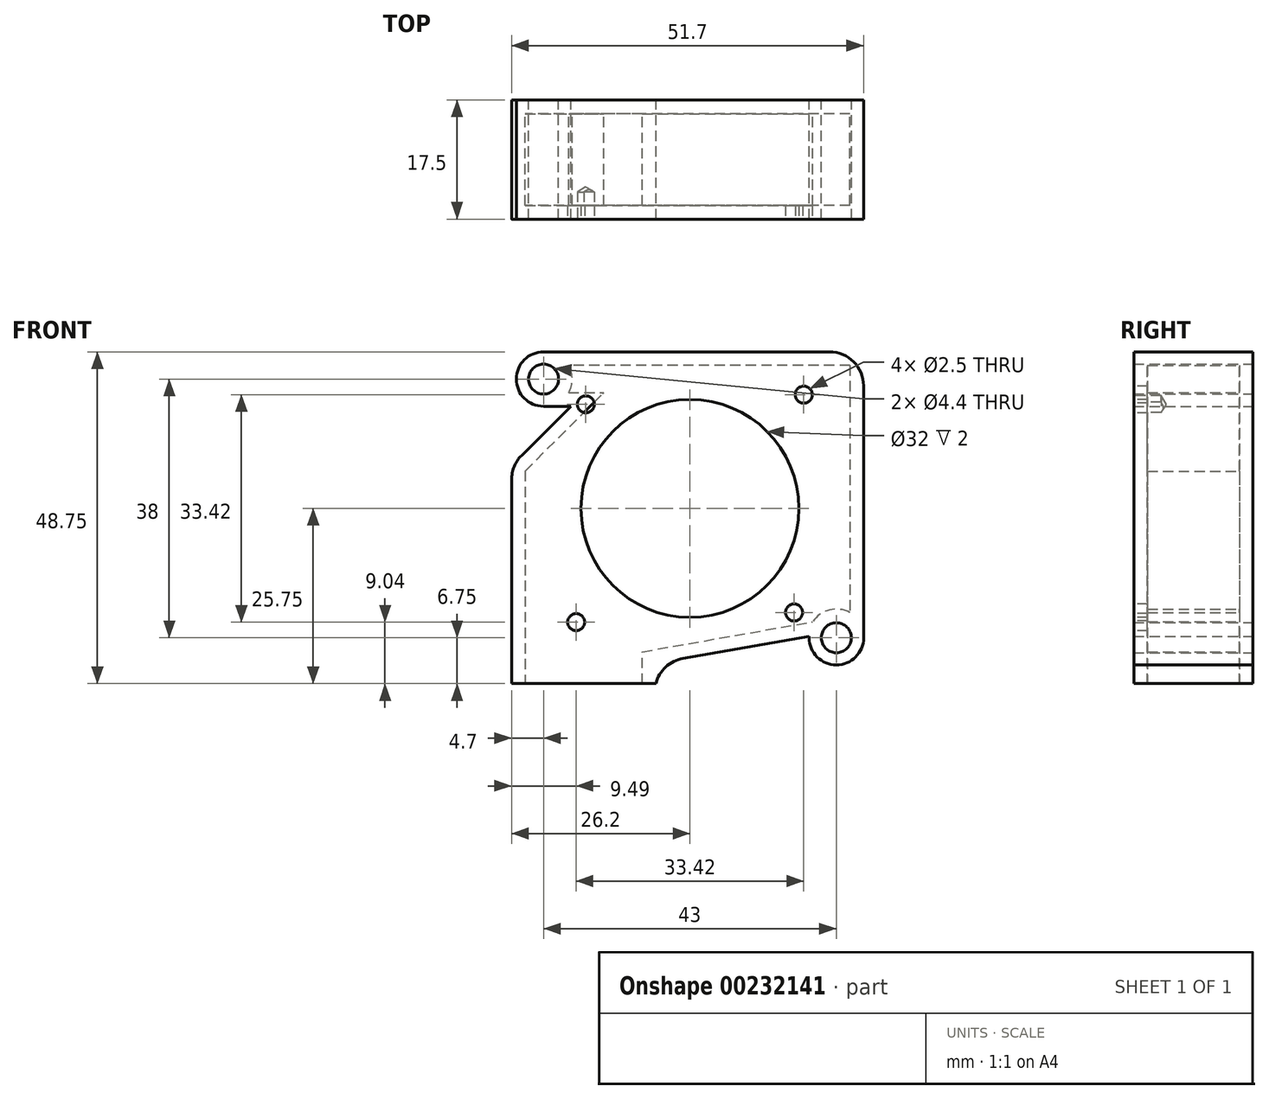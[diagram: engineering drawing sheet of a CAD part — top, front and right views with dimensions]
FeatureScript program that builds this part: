
annotation { "Feature Type Name" : "Feature", "Feature Type Description" : "" }
export const myFeature = defineFeature(function(context is Context, id is Id, definition is map)
    precondition{}
    {
        {
            var Q0;
            Q0=qCreatedBy(makeId("Front.planeOp"),FACE);
            var sketch = newSketch(context, id + "F0", { "sketchPlane" : qUnion([Q0])});
            skLineSegment(sketch, "E0.bottom", {"start": v(25.5, 23) * mm, "end": v(-21.5, 23) * mm});
            skLineSegment(sketch, "E0.left", {"start": v(25.5, 23) * mm, "end": v(25.5, -19) * mm});
            skPoint(sketch, "E0.middle", {"position": v(0, 0) * mm});
            skLineSegment(sketch, "E1.top", {"start": v(-21.5, 15) * mm, "end": v(17.5, 15) * mm});
            skLineSegment(sketch, "E1.right", {"start": v(17.5, -19) * mm, "end": v(17.5, 15) * mm});
            skCircle(sketch, "E2", {"center": v(-21.5, 19) * mm, "radius": 2.2 * mm});
            skCircle(sketch, "E3.MirrorC", {"center": v(21.5, -19) * mm, "radius": 2.2 * mm});
            skArc(sketch, "E4", {"start": v(-21.5, 23) * mm, "mid": v(-25.5, 19) * mm, "end": v(-21.5, 15) * mm});
            skPoint(sketch, "E5.orphan", {"position": v(-25.5, 23) * mm});
            skArc(sketch, "E6", {"start": v(17.5, -19) * mm, "mid": v(21.5, -23) * mm, "end": v(25.5, -19) * mm});
            skPoint(sketch, "E7.orphan", {"position": v(25.5, -23) * mm});
            skSolve(sketch);
        }
        {
            var Q0;
            Q0=makeQuery(id+"F0.imprint","IMPRINT",FACE,{"disambiguationData":[TD([[makeQuery(id+"F0.imprint","IMPRINT",EDGE,{"derivedFrom":sQuery(id+"F0.wireOp",EDGE,"E0.bottom")}),1.0]])]});
            extrude(context, id + "F1", {"entities" : qUnion([Q0]), "depth" : 17.5 * mm});
        }
        {
            var Q0;
            Q0=qCreatedBy(makeId("Front.planeOp"),FACE);
            var sketch = newSketch(context, id + "F2", { "sketchPlane" : qUnion([Q0])});
            skPoint(sketch, "E8.0", {"position": v(17.5, 15) * mm});
            skLineSegment(sketch, "E9.bottom", {"start": v(17.5, 15) * mm, "end": v(-17.5, 15) * mm});
            skLineSegment(sketch, "E9.top", {"start": v(-5, -25.75) * mm, "end": v(-26.2, -25.75) * mm});
            skLineSegment(sketch, "E9.left", {"start": v(17.5, 15) * mm, "end": v(17.5, -18.78) * mm});
            skLineSegment(sketch, "E9.right", {"start": v(-26.2, 6.3) * mm, "end": v(-26.2, -25.75) * mm});
            skLineSegment(sketch, "E10", {"start": v(-5, -25.75) * mm, "end": v(-5, -22.75) * mm});
            skLineSegment(sketch, "E11", {"start": v(-5, -22.75) * mm, "end": v(17.5, -18.78) * mm});
            skLineSegment(sketch, "E12", {"start": v(-26.2, 6.3) * mm, "end": v(-17.5, 15) * mm});
            skSolve(sketch);
        }
        {
            var Q0;
            Q0=makeQuery(id+"F2.imprint","IMPRINT",FACE,{"disambiguationData":[TD([[makeQuery(id+"F2.imprint","IMPRINT",EDGE,{"derivedFrom":sQuery(id+"F2.wireOp",EDGE,"E9.bottom")}),1.0]])]});
            var Q1;
            Q1=makeQuery(id+"F1.opExtrude","CAP_FACE",FACE,{"disambiguationData":[OSD([sQuery(id+"F0.wireOp",EDGE,"E0.bottom"),sQuery(id+"F0.wireOp",EDGE,"E0.left"),sQuery(id+"F0.wireOp",EDGE,"E1.top"),sQuery(id+"F0.wireOp",EDGE,"E1.right"),sQuery(id+"F0.wireOp",EDGE,"E2"),sQuery(id+"F0.wireOp",EDGE,"E3.MirrorC"),sQuery(id+"F0.wireOp",EDGE,"E4"),sQuery(id+"F0.wireOp",EDGE,"E6")])],"isStart":false});
            extrude(context, id + "F3", {"entities" : qUnion([Q0]), "operationType" : NewBodyOperationType.ADD, "endBound" : BoundingType.UP_TO_SURFACE, "endBoundEntityFace" : qUnion([Q1]), "depth" : 25 * mm});
        }
        {
            var Q0;
            Q0=makeQuery(id+"F3.opExtrude","SWEPT_FACE",FACE,{"disambiguationData":[OSD([sQuery(id+"F2.wireOp",EDGE,"E9.top")])]});
            shell(context, id + "F4", {"entities" : qUnion([Q0]), "thickness" : 2 * mm});
        }
        {
            var Q0;
            Q0=makeQuery(id+"F3.opExtrude","SWEPT_EDGE",EDGE,{"disambiguationData":[OSD([sQuery(id+"F2.wireOp",EDGE,"E9.right"),sQuery(id+"F2.wireOp",EDGE,"E12")])]});
            var Q1;
            Q1=makeQuery(id+"F3.opExtrude","SWEPT_EDGE",EDGE,{"disambiguationData":[OSD([sQuery(id+"F2.wireOp",EDGE,"E9.bottom"),sQuery(id+"F2.wireOp",EDGE,"E12")])]});
            var Q2;
            Q2=makeQuery(id+"F3.opExtrude","SWEPT_EDGE",EDGE,{"disambiguationData":[OSD([sQuery(id+"F2.wireOp",EDGE,"E9.left"),sQuery(id+"F2.wireOp",EDGE,"E11")])]});
            var Q3;
            Q3=makeQuery(id+"F1.opExtrude","SWEPT_EDGE",EDGE,{"disambiguationData":[OSD([sQuery(id+"F0.wireOp",EDGE,"E0.bottom"),sQuery(id+"F0.wireOp",EDGE,"E0.left")])]});
            var Q4;
            Q4=makeQuery(id+"F3.opExtrude","SWEPT_EDGE",EDGE,{"disambiguationData":[OSD([sQuery(id+"F2.wireOp",EDGE,"E10"),sQuery(id+"F2.wireOp",EDGE,"E11")])]});
            fillet(context, id + "F5", {"entities" : qUnion([Q0, Q1, Q2, Q3, Q4]), "radius" : 5 * mm, "tangentPropagation" : true, "allowEdgeOverflow" : false});
        }
        {
            var Q0;
            {var subQ0=sQuery(id+"F0.wireOp",EDGE,"E6");var subQ1=sQuery(id+"F0.wireOp",EDGE,"E4");var subQ2=sQuery(id+"F0.wireOp",EDGE,"E3.MirrorC");var subQ3=sQuery(id+"F0.wireOp",EDGE,"E2");var subQ4=sQuery(id+"F0.wireOp",EDGE,"E1.right");var subQ5=sQuery(id+"F0.wireOp",EDGE,"E1.top");var subQ6=sQuery(id+"F0.wireOp",EDGE,"E0.left");var subQ7=sQuery(id+"F0.wireOp",EDGE,"E0.bottom");Q0=makeQuery(id+"F3.boolean.opBoolean","MERGE",FACE,{"derivedFrom":[makeQuery(id+"F1.opExtrude","CAP_FACE",FACE,{"disambiguationData":[OSD([subQ7,subQ6,subQ5,subQ4,subQ3,subQ2,subQ1,subQ0])],"isStart":false}),makeQuery(id+"F3.opExtrude","CAP_FACE",FACE,{"disambiguationData":[OSD([subQ7,subQ6,subQ5,subQ4,subQ3,subQ2,subQ1,subQ0])],"isStart":false})]});}
            var sketch = newSketch(context, id + "F6", { "sketchPlane" : qUnion([Q0])});
            skPoint(sketch, "E13", {"position": v(0, 0) * mm});
            skLineSegment(sketch, "E14", {"start": v(0, 0) * mm, "end": v(-21.63, -21.63) * mm, "construction": true});
            skLineSegment(sketch, "E15", {"start": v(0, 0) * mm, "end": v(24.58, -24.58) * mm, "construction": true});
            skLineSegment(sketch, "E16", {"start": v(0, 0) * mm, "end": v(-20.98, 20.98) * mm, "construction": true});
            skLineSegment(sketch, "E17", {"start": v(0, 0) * mm, "end": v(27.65, 27.65) * mm, "construction": true});
            skPoint(sketch, "E18", {"position": v(-15.3, 15.3) * mm});
            skPoint(sketch, "E19", {"position": v(16.7, 16.7) * mm});
            skPoint(sketch, "E20", {"position": v(15.3, -15.3) * mm});
            skPoint(sketch, "E21", {"position": v(-16.7, -16.7) * mm});
            skSolve(sketch);
        }
        {
            var Q0;
            Q0=sQuery(id+"F6.wireOp",VERTEX,"E13");
            var Q1;
            Q1=makeQuery(id+"F1.opExtrude","SWEPT_BODY",BODY,{"disambiguationData":[OSD([sQuery(id+"F0.wireOp",EDGE,"E0.bottom"),sQuery(id+"F0.wireOp",EDGE,"E0.left"),sQuery(id+"F0.wireOp",EDGE,"E1.top"),sQuery(id+"F0.wireOp",EDGE,"E1.right"),sQuery(id+"F0.wireOp",EDGE,"E2"),sQuery(id+"F0.wireOp",EDGE,"E3.MirrorC"),sQuery(id+"F0.wireOp",EDGE,"E4"),sQuery(id+"F0.wireOp",EDGE,"E6")])]});
            hole(context, id + "F7", {"style" : HoleStyle.SIMPLE, "endStyle" : HoleEndStyle.BLIND, "holeDiameter" : 32 * mm, "holeDepth" : 4 * mm, "startFromSketch" : true, "locations" : qUnion([Q0]), "scope" : qUnion([Q1])});
        }
        {
            var Q0;
            Q0=sQuery(id+"F6.wireOp",VERTEX,"E18");
            var Q1;
            Q1=sQuery(id+"F6.wireOp",VERTEX,"E21");
            var Q2;
            Q2=sQuery(id+"F6.wireOp",VERTEX,"E20");
            var Q3;
            Q3=sQuery(id+"F6.wireOp",VERTEX,"E19");
            var Q4;
            Q4=makeQuery(id+"F1.opExtrude","SWEPT_BODY",BODY,{"disambiguationData":[OSD([sQuery(id+"F0.wireOp",EDGE,"E0.bottom"),sQuery(id+"F0.wireOp",EDGE,"E0.left"),sQuery(id+"F0.wireOp",EDGE,"E1.top"),sQuery(id+"F0.wireOp",EDGE,"E1.right"),sQuery(id+"F0.wireOp",EDGE,"E2"),sQuery(id+"F0.wireOp",EDGE,"E3.MirrorC"),sQuery(id+"F0.wireOp",EDGE,"E4"),sQuery(id+"F0.wireOp",EDGE,"E6")])]});
            hole(context, id + "F8", {"style" : HoleStyle.SIMPLE, "endStyle" : HoleEndStyle.BLIND, "holeDiameter" : 2.5 * mm, "holeDepth" : 4 * mm, "startFromSketch" : true, "locations" : qUnion([Q0, Q1, Q2, Q3]), "scope" : qUnion([Q4])});
        }
    });
